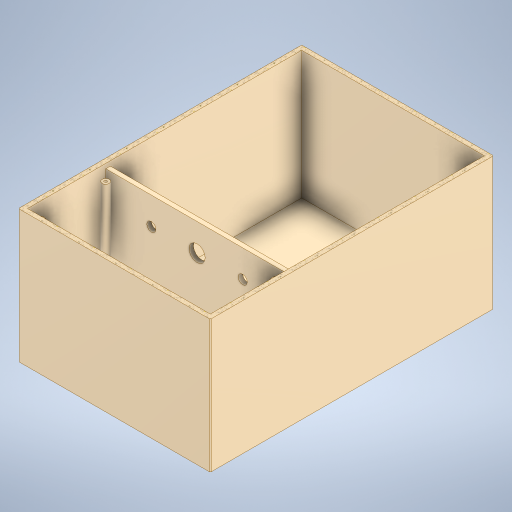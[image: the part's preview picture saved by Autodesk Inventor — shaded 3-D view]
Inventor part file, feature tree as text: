
AUTODESK INVENTOR PART (.ipt)
format: ipt  version: 2023.1 (Build 271208000, 208)  size: 292,864 bytes
history: native  units: in
note: dims shown in document units (in); Inventor stores cm internally (conversion verified against a paired STEP export)
features: extrude x5, sketch x5, other x1, shell x1, chamfer x1
ambient origin geometry x8: Origin, YZ Plane, XZ Plane, XY Plane, X Axis, Y Axis, Z Axis, Center Point
bodies: Body1 (feature_tree)
feature tree (13):
  other  "CrossSection1"
  extrude  "Extrusion3"  Depth=8.2677in
  shell  "Shell1"  Thickness=5.9055in
  extrude  "Extrusion4"  Depth=0.1969in
  sketch  "Sketch6"  dims[d14=0.0197in d15=0.0787in d16=-0.1969in d17=0.7874in]
  chamfer  "Chamfer1"  Distance=7.874in
  extrude  "Extrusion5"  Depth=1.1811in TaperAngle=45.0deg
  extrude  "Extrusion6"  Depth=0.3937in TaperAngle=0.0deg
  extrude  "Extrusion7"  Depth=1.1811in
  sketch  "Sketch4"  dims[d9=12.2047in d10=8.2677in d11=5.9055in]
  sketch  "Sketch5"  dims[d12=0.0in d13=0.1969in]
  sketch  "Sketch7"  dims[d18=0.1969in]
  sketch  "Sketch8"  dims[d19=5.315in d20=7.874in d21=0.0in d32=0.0394in d33=0.0787in d34=45.0deg d35=0.3937in d36=0.0in d37=0.315in d38=0.315in d39=0.315in d40=0.315in d41=0.2756in d42=0.2756in d43=0.2756in d44=0.2756in d45=0.2756in d46=0.2756in d47=0.2756in d48=0.2756in d49=5.1181in d50=0.0in d51=0.1181in d52=0.1181in d53=0.1181in d54=0.1181in d55=1.1811in d56=0.0in d4=0.5in d5=0.0344in d6=0.5in d7=0.0344in]
